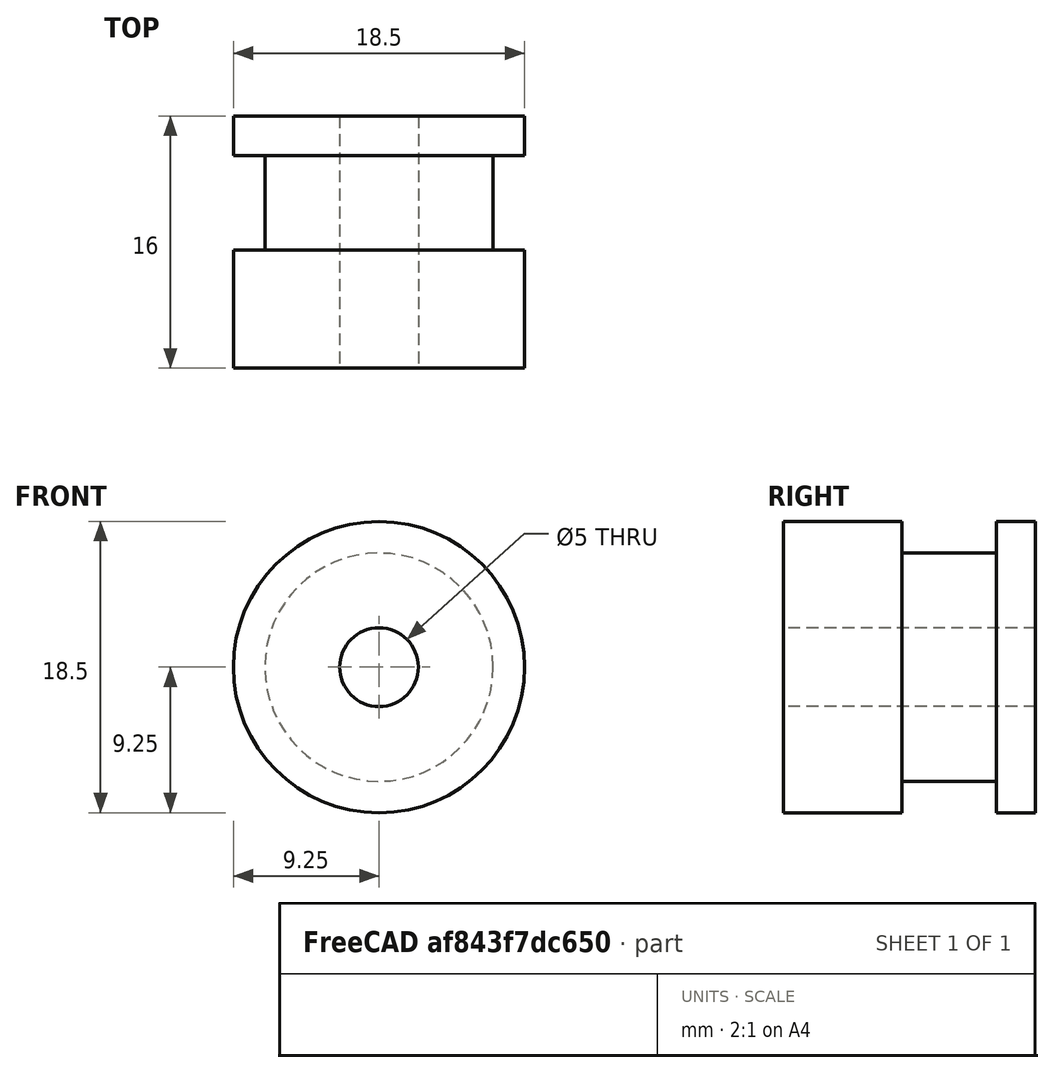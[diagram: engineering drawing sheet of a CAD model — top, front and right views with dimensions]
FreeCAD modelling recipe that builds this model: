
FCSTD DOCUMENT  (FreeCAD 0.18R)
Label: timing-gear-16mm
License: All rights reserved
LicenseURL: http://en.wikipedia.org/wiki/All_rights_reserved
objects: Sketcher::SketchObject×1, PartDesign::Revolution×1, PartDesign::Body×1
note: 4 computed .brp shape members not serialized (recipe doc carries the construction recipe); baked Part::Feature solids carry a one-line shape summary decoded from their .brp

FEATURE [Sketcher::SketchObject] Sketch002
  MapMode = 5
  Support = -> [XY_Plane003]
  sketch-geometry (8):
    g0: LineSegment StartX=-9.25 StartY=16 StartZ=0 EndX=-2.5 EndY=16 EndZ=0
    g1: LineSegment StartX=-9.25 StartY=0 StartZ=0 EndX=-2.5 EndY=0 EndZ=0
    g2: LineSegment StartX=-2.5 StartY=16 StartZ=0 EndX=-2.5 EndY=0 EndZ=0
    g3: LineSegment StartX=-9.25 StartY=0 StartZ=0 EndX=-9.25 EndY=7.5 EndZ=0
    g4: LineSegment StartX=-9.25 StartY=7.5 StartZ=0 EndX=-7.25 EndY=7.5 EndZ=0
    g5: LineSegment StartX=-7.25 StartY=7.5 StartZ=0 EndX=-7.25 EndY=13.5 EndZ=0
    g6: LineSegment StartX=-7.25 StartY=13.5 StartZ=0 EndX=-9.25 EndY=13.5 EndZ=0
    g7: LineSegment StartX=-9.25 StartY=16 StartZ=0 EndX=-9.25 EndY=13.5 EndZ=0
  constraints (24):
    c: Horizontal(g0)
    c: DistanceX(g0,g0) = 6.75
    c: PointOnObject(g1,g-1)
    c: PointOnObject(g1,g-1)
    c: DistanceX(g1,g0) = 0
    c: Coincident(g2,g0)
    c: Coincident(g1,g2)
    c: Equal(g0,g1)
    c: DistanceX(g1,g-1) = 2.5
    c: Coincident(g3,g1)
    c: Vertical(g3)
    c: DistanceY(g3,g3) = 7.5
    c: Coincident(g4,g3)
    c: Horizontal(g4)
    c: DistanceX(g4,g4) = 2
    c: Coincident(g5,g4)
    c: Vertical(g5)
    c: DistanceY(g5,g5) = 6
    c: Coincident(g6,g5)
    c: Horizontal(g6)
    c: Equal(g6,g4)
    c: Coincident(g7,g0)
    c: Coincident(g7,g6)
    c: DistanceY(g-1,g0) = 16
FEATURE [PartDesign::Revolution] Revolution
  Angle = 360
  Axis = (0,1,0)
  Base = (0,0,0)
  Profile = -> Sketch002
  ReferenceAxis = -> Sketch002 [V_Axis]
FEATURE [PartDesign::Body] Body003  label="timing-gear-16mm"
  Group = -> [Sketch002,Revolution]
  Origin = -> Origin003
  Tip = -> Revolution
